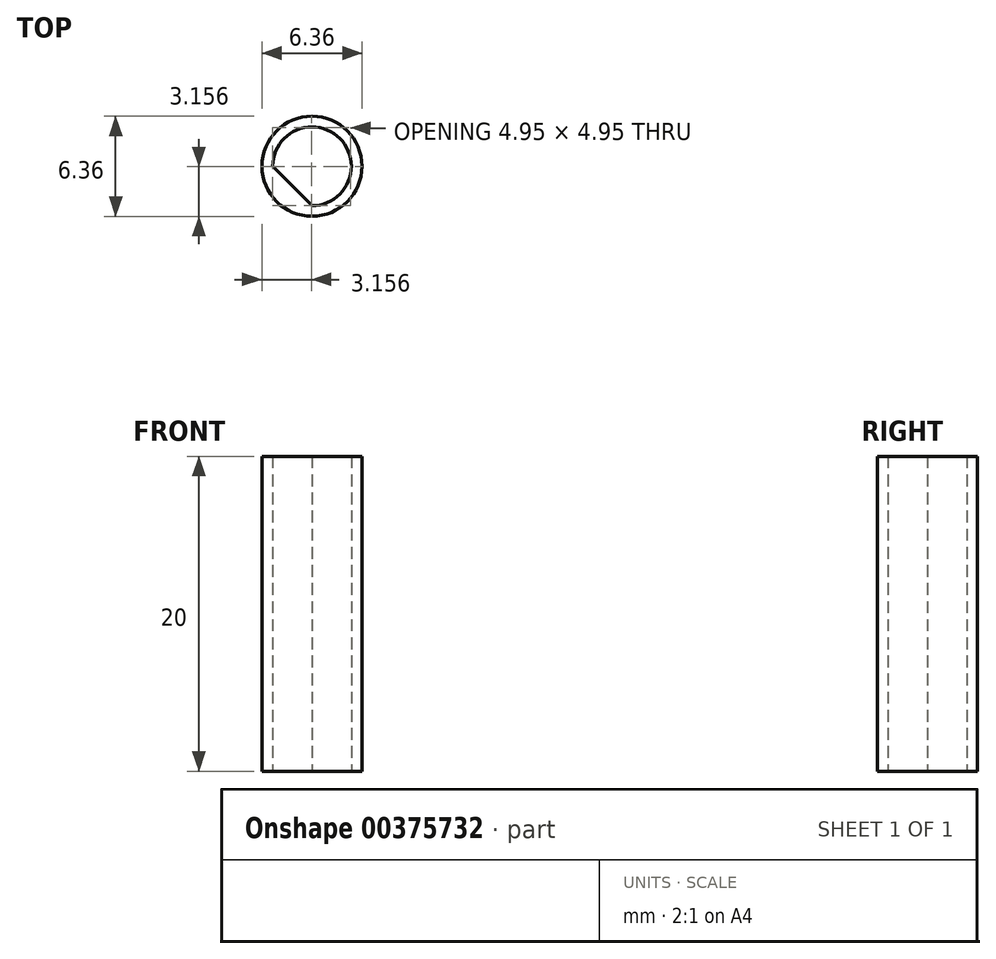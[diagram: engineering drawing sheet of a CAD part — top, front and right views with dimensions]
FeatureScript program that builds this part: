
annotation { "Feature Type Name" : "Feature", "Feature Type Description" : "" }
export const myFeature = defineFeature(function(context is Context, id is Id, definition is map)
    precondition{}
    {
        {
            var Q0;
            Q0=qCreatedBy(makeId("Top.planeOp"),FACE);
            var sketch = newSketch(context, id + "F0", { "sketchPlane" : qUnion([Q0])});
            skCircle(sketch, "E0", {"center": v(0, 0) * mm, "radius": 3.18 * mm});
            skArc(sketch, "E1", {"start": v(0, -2.5) * mm, "mid": v(1.77, 1.77) * mm, "end": v(-2.5, 0) * mm});
            skLineSegment(sketch, "E2", {"start": v(-2.5, 0) * mm, "end": v(0, -2.5) * mm});
            skSolve(sketch);
        }
        {
            var Q0;
            Q0=makeQuery(id+"F0.imprint","IMPRINT",FACE,{"disambiguationData":[TD([[makeQuery(id+"F0.imprint","IMPRINT",EDGE,{"derivedFrom":sQuery(id+"F0.wireOp",EDGE,"E0")}),1.0]])]});
            extrude(context, id + "F1", {"entities" : qUnion([Q0]), "depth" : 20 * mm});
        }
    });
